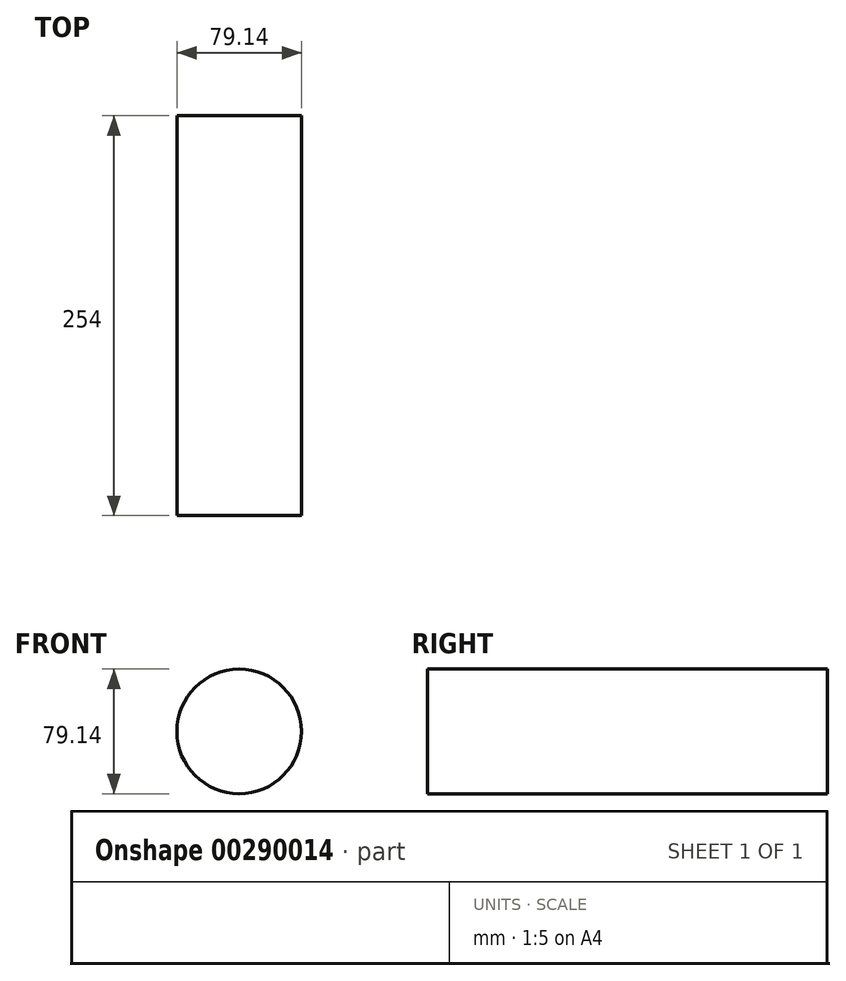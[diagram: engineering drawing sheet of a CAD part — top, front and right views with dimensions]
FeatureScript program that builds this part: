
annotation { "Feature Type Name" : "Feature", "Feature Type Description" : "" }
export const myFeature = defineFeature(function(context is Context, id is Id, definition is map)
    precondition{}
    {
        {
            var Q0;
            Q0=qCreatedBy(makeId("Front.planeOp"),FACE);
            var sketch = newSketch(context, id + "F0", { "sketchPlane" : qUnion([Q0])});
            skCircle(sketch, "E0", {"center": v(0, 0) * mm, "radius": 38.23 * mm});
            skCircle(sketch, "E1", {"center": v(0, 0) * mm, "radius": 39.57 * mm});
            skSolve(sketch);
        }
        {
            var Q0;
            Q0 = qSketchRegion(id + "F0", true);
            var Q1;
            Q1=makeQuery(id+"F0.imprint","IMPRINT",FACE,{"disambiguationData":[TD([[makeQuery(id+"F0.imprint","IMPRINT",EDGE,{"derivedFrom":sQuery(id+"F0.wireOp",EDGE,"E0")}),1.0]])]});
            extrude(context, id + "F1", {"entities" : qUnion([Q0, Q1]), "depth" : 254 * mm});
        }
    });
